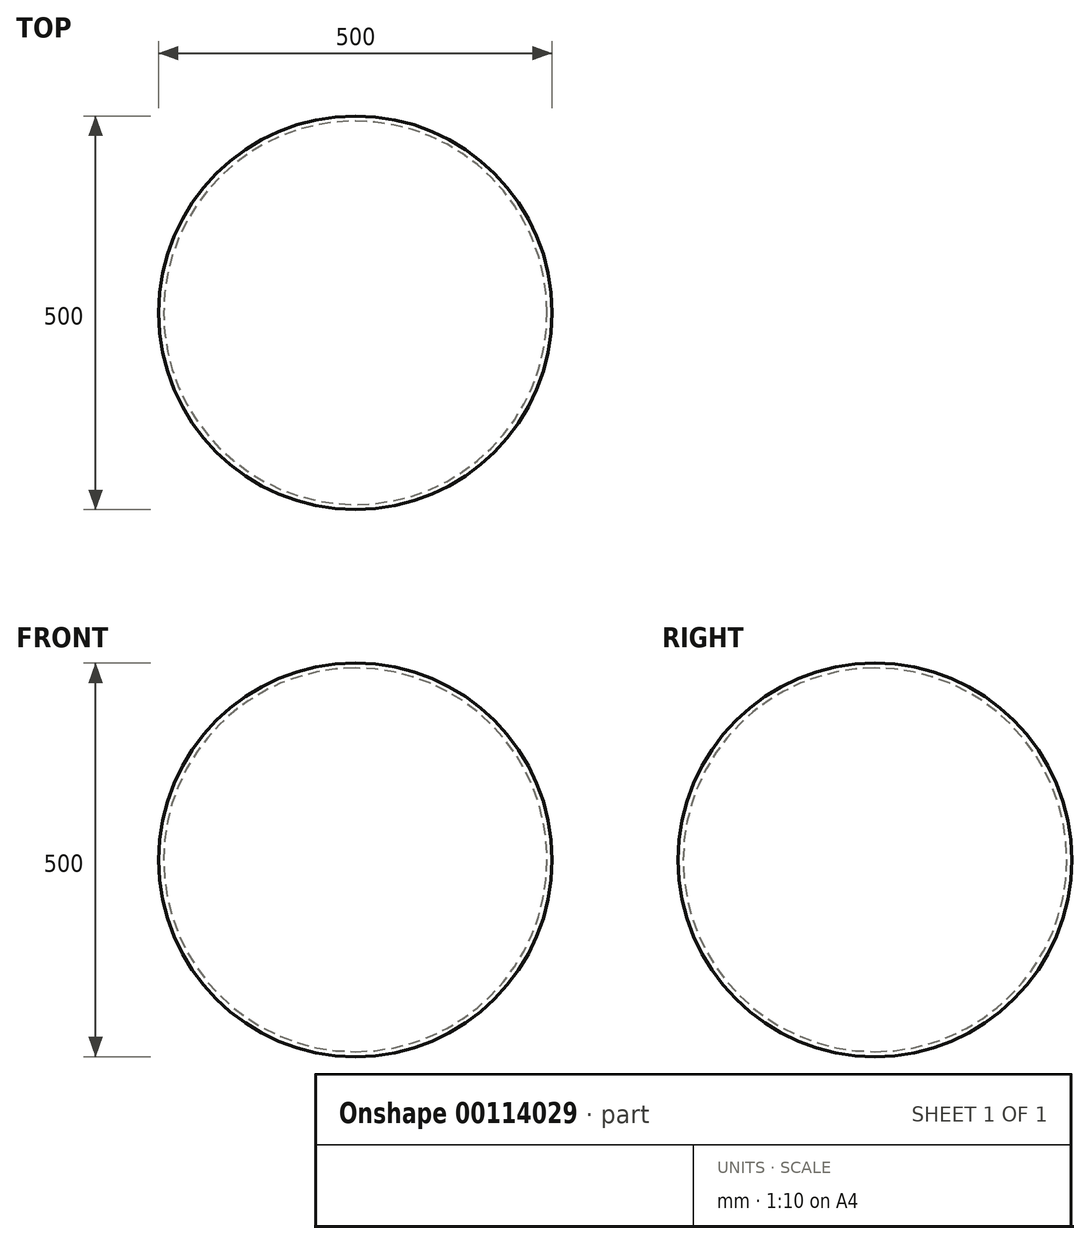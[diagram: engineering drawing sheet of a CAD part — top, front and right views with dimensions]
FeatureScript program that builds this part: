
annotation { "Feature Type Name" : "Feature", "Feature Type Description" : "" }
export const myFeature = defineFeature(function(context is Context, id is Id, definition is map)
    precondition{}
    {
        {
            var Q0;
            Q0=qCreatedBy(makeId("Front.planeOp"),FACE);
            var sketch = newSketch(context, id + "F0", { "sketchPlane" : qUnion([Q0])});
            skArc(sketch, "E0", {"start": v(0, 250) * mm, "mid": v(-250, 0) * mm, "end": v(0, -250) * mm});
            skArc(sketch, "E1", {"start": v(0, 243.59) * mm, "mid": v(-243.59, 0) * mm, "end": v(0, -243.59) * mm});
            skLineSegment(sketch, "E2", {"start": v(0, -308.93) * mm, "end": v(0, 324.98) * mm, "construction": true});
            skLineSegment(sketch, "E3", {"start": v(0, 250) * mm, "end": v(0, -250) * mm});
            skSolve(sketch);
        }
        {
            var Q0;
            Q0=makeQuery(id+"F0.imprint","IMPRINT",FACE,{"disambiguationData":[TD([[makeQuery(id+"F0.imprint","IMPRINT",EDGE,{"derivedFrom":sQuery(id+"F0.wireOp",EDGE,"E0")}),1.0]])]});
            var Q1;
            Q1=sQuery(id+"F0.wireOp",EDGE,"E2");
            revolve(context, id + "F1", {"entities" : qUnion([Q0]), "axis" : qUnion([Q1]), "revolveType" : RevolveType.ONE_DIRECTION, "angle" : 360 * degree});
        }
    });
